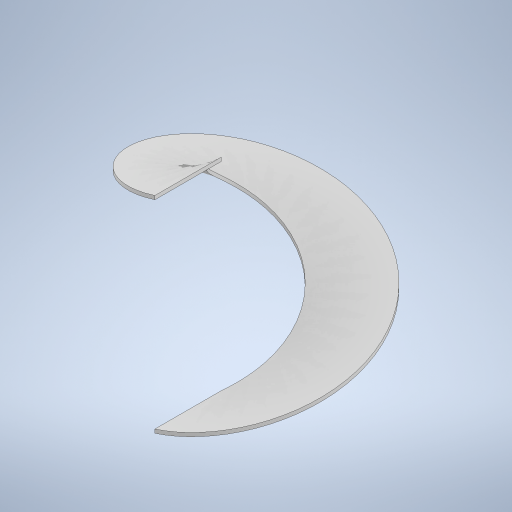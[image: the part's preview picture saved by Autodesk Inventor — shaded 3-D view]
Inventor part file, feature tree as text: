
AUTODESK INVENTOR PART (.ipt)
format: ipt  version: 2024 (Build 280153000, 153)  size: 250,368 bytes
history: native  units: mm
features: sketch x3, plane x1, helix x1
ambient origin geometry x8: Origin, YZ Plane, XZ Plane, XY Plane, X Axis, Y Axis, Z Axis, Center Point
bodies: Solid1 (feature_tree)
feature tree (5):
  sketch  "Sketch1"  dims[d1=3.2mm]
  plane  "Work Plane1"
  sketch  "Sketch2"  dims[d2=175.0mm]
  helix  "Coil1"  [1 undecoded]
  sketch  "Sketch3"  dims[d3=175.0mm d4=175.0mm d5=10.0mm d6=10.0mm d7=0.0mm d8=90.0deg d9=90.0deg d10=0.0mm d11=0.0mm d12=60.3mm d13=30.15mm d14=87.5mm d15=3.2mm]
note: 1 required parameter value undecoded (feature->parameter linkage not recoverable at this tier; creation-order binding heuristic only, values carry confidence <= 0.55)
